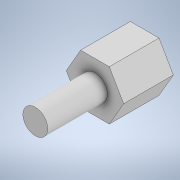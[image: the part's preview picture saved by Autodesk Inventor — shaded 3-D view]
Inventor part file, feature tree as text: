
AUTODESK INVENTOR PART (.ipt)
format: ipt  version: 2021 (Build 250183000, 183)  size: 114,688 bytes
history: native  units: mm
features: extrude x4, sketch x4, projected_geometry x1
ambient origin geometry x8: Origin, YZ Plane, XZ Plane, XY Plane, X Axis, Y Axis, Z Axis, Center Point
bodies: Solid1 (feature_tree)
feature tree (9):
  extrude  "Extrusion1"  Depth=5.0mm TaperAngle=0.0deg
  extrude  "Extrusion3"  Depth=7.0mm TaperAngle=0.0deg
  extrude  "Extrusion4"  Depth=6.0mm TaperAngle=0.0deg
  extrude  "Extrusion5"  [1 undecoded]
  sketch  "Sketch1"  dims[d0=5.0mm d1=5.0mm d2=0.0mm]
  sketch  "Sketch3"  dims[d6=2.5mm d7=7.0mm d8=0.0mm]
  sketch  "Sketch4"  dims[d9=2.5mm d10=6.0mm d11=0.0mm]
  sketch  "Sketch5"  dims[d12=3.0mm d13=0.0mm]
  projected_geometry  "Projected Loop1"
note: 1 required parameter value undecoded (feature->parameter linkage not recoverable at this tier; creation-order binding heuristic only, values carry confidence <= 0.55)
